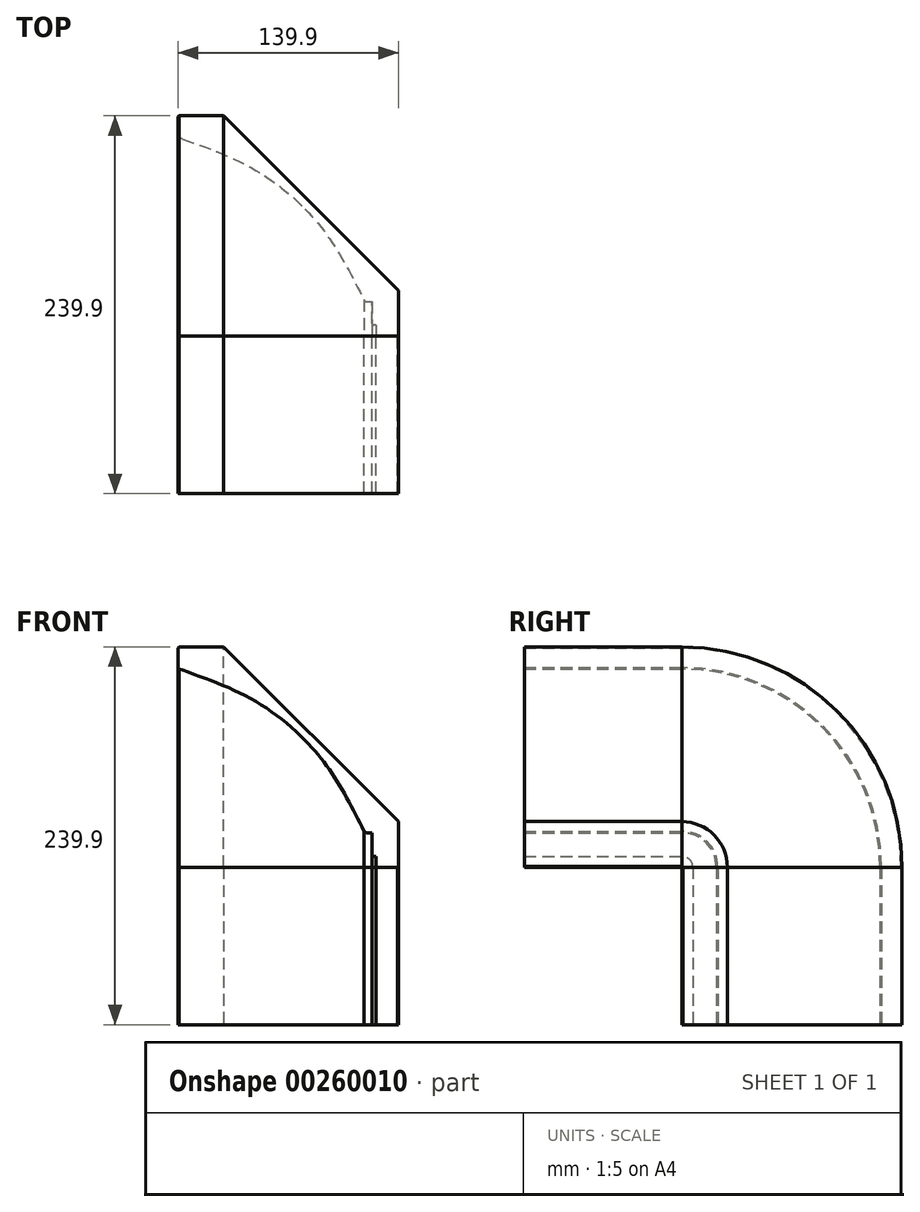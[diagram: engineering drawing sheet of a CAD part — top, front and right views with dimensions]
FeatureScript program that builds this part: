
annotation { "Feature Type Name" : "Feature", "Feature Type Description" : "" }
export const myFeature = defineFeature(function(context is Context, id is Id, definition is map)
    precondition{}
    {
        {
            var Q0;
            Q0=qCreatedBy(makeId("Front.planeOp"),FACE);
            var sketch = newSketch(context, id + "F0", { "sketchPlane" : qUnion([Q0])});
            skFitSpline(sketch, "E0", {"points": [v(-139.2, -14.02) * mm, v(-90.07, -34.93) * mm, v(-48.93, -71.02) * mm, v(-21.8, -117) * mm]});
            skLineSegment(sketch, "E1", {"start": v(-0.67, -139.9) * mm, "end": v(-13, -139.9) * mm});
            skLineSegment(sketch, "E2", {"start": v(-55.47, -55.47) * mm, "end": v(-63.84, -63.84) * mm});
            skLineSegment(sketch, "E3", {"start": v(-139.9, -0.67) * mm, "end": v(-139.9, -13.01) * mm});
            skLineSegment(sketch, "E4", {"start": v(0, -110.95) * mm, "end": v(0, -139.23) * mm});
            skLineSegment(sketch, "E5", {"start": v(-110.95, 0) * mm, "end": v(-139.23, 0) * mm});
            skLineSegment(sketch, "E6", {"start": v(-0.67, -139.9) * mm, "end": v(0, -139.23) * mm});
            skLineSegment(sketch, "E7", {"start": v(-139.23, 0) * mm, "end": v(-139.9, -0.67) * mm});
            skLineSegment(sketch, "E8", {"start": v(-110.95, 0) * mm, "end": v(0, -110.95) * mm});
            skLineSegment(sketch, "E9", {"start": v(-139.81, -13.56) * mm, "end": v(-139.77, -13.6) * mm});
            skLineSegment(sketch, "E10", {"start": v(-3.21, -128.98) * mm, "end": v(-12.2, -137.97) * mm});
            skLineSegment(sketch, "E11.trimOffspring", {"start": v(-14.13, -132.97) * mm, "end": v(-15.64, -132.97) * mm});
            skLineSegment(sketch, "E12", {"start": v(-20.08, -117.98) * mm, "end": v(-16.64, -117.98) * mm});
            skArc(sketch, "E13", {"start": v(-21.8, -117) * mm, "mid": v(-21.07, -117.72) * mm, "end": v(-20.08, -117.98) * mm});
            skLineSegment(sketch, "E14", {"start": v(-139.9, -13.01) * mm, "end": v(-139.9, -13.12) * mm});
            skArc(sketch, "E15", {"start": v(-139.9, -13.01) * mm, "mid": v(-139.75, -13.6) * mm, "end": v(-139.29, -13.98) * mm});
            skLineSegment(sketch, "E16", {"start": v(-139.2, -14.02) * mm, "end": v(-139.29, -13.98) * mm});
            skLineSegment(sketch, "E17", {"start": v(-137.41, -15.48) * mm, "end": v(-137.2, -14.5) * mm});
            skLineSegment(sketch, "E18", {"start": v(-139.37, -14) * mm, "end": v(-14.37, -139) * mm, "construction": true});
            skLineSegment(sketch, "E19", {"start": v(-16.64, -131.97) * mm, "end": v(-16.64, -117.98) * mm});
            skLineSegment(sketch, "E20.MirrorCS", {"start": v(-14.13, -132.97) * mm, "end": v(-14.13, -138.77) * mm});
            skLineSegment(sketch, "E21", {"start": v(-12.67, -140.7) * mm, "end": v(-10.57, -142.8) * mm});
            skPoint(sketch, "E22.orphan", {"position": v(-14.13, -138.77) * mm});
            skPoint(sketch, "E23", {"position": v(-13, -138.77) * mm});
            skPoint(sketch, "E24", {"position": v(-13, -139.9) * mm});
            skArc(sketch, "E25", {"start": v(-14.13, -138.77) * mm, "mid": v(-13.8, -139.57) * mm, "end": v(-13, -139.9) * mm});
            skPoint(sketch, "E26.visualSharp", {"position": v(-16.64, -132.97) * mm});
            skArc(sketch, "E26.filletArc", {"start": v(-16.64, -131.97) * mm, "mid": v(-16.35, -132.67) * mm, "end": v(-15.64, -132.97) * mm});
            skLineSegment(sketch, "E27", {"start": v(-110.95, 0) * mm, "end": v(0, 0) * mm, "construction": true});
            skLineSegment(sketch, "E28", {"start": v(0, -110.95) * mm, "end": v(0, 0) * mm, "construction": true});
            skSolve(sketch);
        }
        {
            var Q0;
            Q0=makeQuery(id+"F0.imprint","IMPRINT",FACE,{"disambiguationData":[TD([[makeQuery(id+"F0.imprint","IMPRINT",EDGE,{"derivedFrom":sQuery(id+"F0.wireOp",EDGE,"E1")}),-1.0]])]});
            var Q1;
            {var subQ0=sQuery(id+"F0.wireOp",EDGE,"E2");Q1=makeQuery(id+"F0.imprint","IMPRINT",FACE,{"disambiguationData":[TD([[makeQuery(id+"F0.imprint","IMPRINT",EDGE,{"derivedFrom":subQ0}),-1.0]])]});}
            extrude(context, id + "F1", {"entities" : qUnion([Q0, Q1]), "depth" : 100 * mm});
        }
        {
            var Q0;
            Q0=makeQuery(id+"F1.opExtrude","CAP_FACE",FACE,{"disambiguationData":[OSD([sQuery(id+"F0.wireOp",EDGE,"E0"),sQuery(id+"F0.wireOp",EDGE,"E1"),sQuery(id+"F0.wireOp",EDGE,"E3"),sQuery(id+"F0.wireOp",EDGE,"E4"),sQuery(id+"F0.wireOp",EDGE,"E5"),sQuery(id+"F0.wireOp",EDGE,"E6"),sQuery(id+"F0.wireOp",EDGE,"E7"),sQuery(id+"F0.wireOp",EDGE,"E8"),sQuery(id+"F0.wireOp",EDGE,"E11.trimOffspring"),sQuery(id+"F0.wireOp",EDGE,"E12"),sQuery(id+"F0.wireOp",EDGE,"E13"),sQuery(id+"F0.wireOp",EDGE,"E14"),sQuery(id+"F0.wireOp",EDGE,"E15"),sQuery(id+"F0.wireOp",EDGE,"E16"),sQuery(id+"F0.wireOp",EDGE,"E19"),sQuery(id+"F0.wireOp",EDGE,"E20.MirrorCS"),sQuery(id+"F0.wireOp",EDGE,"E25"),sQuery(id+"F0.wireOp",EDGE,"E26.filletArc")])],"isStart":false});
            cPlane(context, id + "F2", {"entities" : qUnion([Q0]), "cplaneType" : CPlaneType.OFFSET, "offset" : 25 * mm, "width" : 150 * mm, "height" : 150 * mm});
        }
        {
            var Q0;
            Q0=makeQuery(id+"F1.opExtrude","SWEPT_BODY",BODY,{"disambiguationData":[OSD([sQuery(id+"F0.wireOp",EDGE,"E0"),sQuery(id+"F0.wireOp",EDGE,"E1"),sQuery(id+"F0.wireOp",EDGE,"E3"),sQuery(id+"F0.wireOp",EDGE,"E4"),sQuery(id+"F0.wireOp",EDGE,"E5"),sQuery(id+"F0.wireOp",EDGE,"E6"),sQuery(id+"F0.wireOp",EDGE,"E7"),sQuery(id+"F0.wireOp",EDGE,"E8"),sQuery(id+"F0.wireOp",EDGE,"E11.trimOffspring"),sQuery(id+"F0.wireOp",EDGE,"E12"),sQuery(id+"F0.wireOp",EDGE,"E13"),sQuery(id+"F0.wireOp",EDGE,"E14"),sQuery(id+"F0.wireOp",EDGE,"E15"),sQuery(id+"F0.wireOp",EDGE,"E16"),sQuery(id+"F0.wireOp",EDGE,"E19"),sQuery(id+"F0.wireOp",EDGE,"E20.MirrorCS"),sQuery(id+"F0.wireOp",EDGE,"E25"),sQuery(id+"F0.wireOp",EDGE,"E26.filletArc")])]});
            var Q1;
            Q1=makeQuery(id+"F1.opExtrude","CAP_EDGE",EDGE,{"disambiguationData":[OSD([sQuery(id+"F0.wireOp",EDGE,"E1")])],"isStart":true});
            transform(context, id + "F3", {"entities" : qUnion([Q0]), "transformType" : TransformType.ROTATION, "transformAxis" : qUnion([Q1]), "angle" : 90 * degree, "makeCopy" : true});
        }
        {
            var Q0;
            Q0=makeQuery(id+"F1.opExtrude","CAP_FACE",FACE,{"disambiguationData":[OSD([sQuery(id+"F0.wireOp",EDGE,"E0"),sQuery(id+"F0.wireOp",EDGE,"E1"),sQuery(id+"F0.wireOp",EDGE,"E3"),sQuery(id+"F0.wireOp",EDGE,"E4"),sQuery(id+"F0.wireOp",EDGE,"E5"),sQuery(id+"F0.wireOp",EDGE,"E6"),sQuery(id+"F0.wireOp",EDGE,"E7"),sQuery(id+"F0.wireOp",EDGE,"E8"),sQuery(id+"F0.wireOp",EDGE,"E11.trimOffspring"),sQuery(id+"F0.wireOp",EDGE,"E12"),sQuery(id+"F0.wireOp",EDGE,"E13"),sQuery(id+"F0.wireOp",EDGE,"E14"),sQuery(id+"F0.wireOp",EDGE,"E15"),sQuery(id+"F0.wireOp",EDGE,"E16"),sQuery(id+"F0.wireOp",EDGE,"E19"),sQuery(id+"F0.wireOp",EDGE,"E20.MirrorCS"),sQuery(id+"F0.wireOp",EDGE,"E25"),sQuery(id+"F0.wireOp",EDGE,"E26.filletArc")])],"isStart":true});
            var Q1;
            Q1=makeQuery(id+"F1.opExtrude","CAP_EDGE",EDGE,{"disambiguationData":[OSD([sQuery(id+"F0.wireOp",EDGE,"E1")])],"isStart":true});
            revolve(context, id + "F4", {"entities" : qUnion([Q0]), "axis" : qUnion([Q1]), "revolveType" : RevolveType.ONE_DIRECTION, "angle" : 90 * degree});
        }
        {
            var Q0;
            Q0=makeQuery(id+"F3.opPattern","COPY",BODY,{"derivedFrom":makeQuery(id+"F1.opExtrude","SWEPT_BODY",BODY,{"disambiguationData":[OSD([sQuery(id+"F0.wireOp",EDGE,"E0"),sQuery(id+"F0.wireOp",EDGE,"E1"),sQuery(id+"F0.wireOp",EDGE,"E3"),sQuery(id+"F0.wireOp",EDGE,"E4"),sQuery(id+"F0.wireOp",EDGE,"E5"),sQuery(id+"F0.wireOp",EDGE,"E6"),sQuery(id+"F0.wireOp",EDGE,"E7"),sQuery(id+"F0.wireOp",EDGE,"E8"),sQuery(id+"F0.wireOp",EDGE,"E11.trimOffspring"),sQuery(id+"F0.wireOp",EDGE,"E12"),sQuery(id+"F0.wireOp",EDGE,"E13"),sQuery(id+"F0.wireOp",EDGE,"E14"),sQuery(id+"F0.wireOp",EDGE,"E15"),sQuery(id+"F0.wireOp",EDGE,"E16"),sQuery(id+"F0.wireOp",EDGE,"E19"),sQuery(id+"F0.wireOp",EDGE,"E20.MirrorCS"),sQuery(id+"F0.wireOp",EDGE,"E25"),sQuery(id+"F0.wireOp",EDGE,"E26.filletArc")])]}),"instanceName":"1"});
            var Q1;
            Q1=makeQuery(id+"F3.opPattern","COPY",VERTEX,{"derivedFrom":makeQuery(id+"F1.opExtrude","CAP_VERTEX",VERTEX,{"disambiguationData":[OSD([sQuery(id+"F0.wireOp",EDGE,"E3"),sQuery(id+"F0.wireOp",EDGE,"E7")])],"isStart":false}),"instanceName":"1"});
            var Q2;
            Q2=makeQuery(id+"F4.opRevolve","CAP_VERTEX",VERTEX,{"disambiguationData":[OSD([sQuery(id+"F0.wireOp",EDGE,"E3"),sQuery(id+"F0.wireOp",EDGE,"E7")])],"isStart":false});
            transform(context, id + "F5", {"entities" : qUnion([Q0]), "transformType" : TransformType.TRANSLATION_ENTITY, "oppositeDirectionEntity" : false, "transformLine" : qUnion([Q1, Q2]), "makeCopy" : false});
        }
    });
